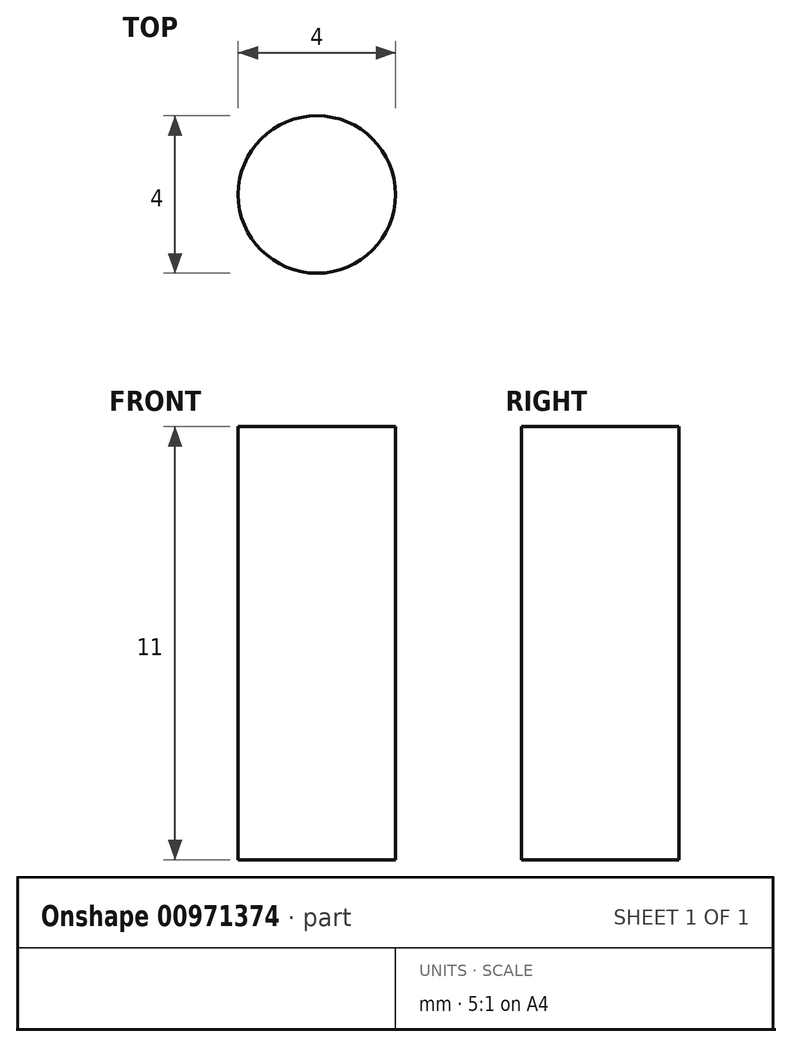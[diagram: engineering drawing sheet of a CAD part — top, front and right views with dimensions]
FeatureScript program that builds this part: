
annotation { "Feature Type Name" : "Feature", "Feature Type Description" : "" }
export const myFeature = defineFeature(function(context is Context, id is Id, definition is map)
    precondition{}
    {
        {
            var Q0;
            Q0=qCreatedBy(makeId("Top.planeOp"),FACE);
            var sketch = newSketch(context, id + "F0", { "sketchPlane" : qUnion([Q0])});
            skCircle(sketch, "E0", {"center": v(0, 0) * mm, "radius": 2 * mm});
            skSolve(sketch);
        }
        {
            var Q0;
            Q0=makeQuery(id+"F0.imprint","IMPRINT",FACE,{"disambiguationData":[TD([[makeQuery(id+"F0.imprint","IMPRINT",EDGE,{"derivedFrom":sQuery(id+"F0.wireOp",EDGE,"E0")}),1.0]])]});
            extrude(context, id + "F1", {"entities" : qUnion([Q0]), "depth" : (2 + 2 + 3 + 2 + 2) * mm, "offsetDistance" : 25 * mm});
        }
    });
